# Revit family: Haworth_JiveTable_PebbleSymmetricalLegs
name_source: partatom
category: Furniture Systems
revit_build: Autodesk Revit 2018 (Build: 20170223_1515(x64)
units: mm (PartAtom-declared; Revit-internal decimal feet)

## family parameters
Always vertical = Yes
Cut with Voids When Loaded = No
OmniClass Number = 23.40.70.14.64.21
OmniClass Title = Systems Furniture
Part Type = Normal
Room Calculation Point = No
Round Connector Dimension = Use Diameter
Shared = No
Work Plane-Based = No

## types (19) — shared parameters
Assembly Code = E2020200
Custom Size = No
Manufacturer = Haworth, Inc.
Max. Height = 29"
Min. Height = 16"
Model = Hawoth Jive
Revision Number = 0
Size = Verify Final Dim. w/ Haworth
Standard Depths = 24, 30, 36, 42, 48, 54, 60 in.
Standard Height = 16, 20, 29 in.
Standard Widths = 24, 30, 36, 42, 48, 54, 60 in.
Table Thickness = 1 3/16"
URL = http://www.haworth.com
URL - Product = http://www.haworth.com
Warranty = http://haworth.com

## per-type parameters (varying)
- 24d 24w 16h - Post Extruded Base - With Glides: 24in x 24in=Yes; 30in x 30in=No; 36in x 36in=No; 42in x 42in=No; 48in x 48in=No; 54in x 54in=No; 60in x 60in=No; Actual Depth=24"; Actual Height=16"; Actual Width=24"; Casters=No; Controls Post Extruded 42d 42w Only=No; Controls Post Round 42d 42w Only=Yes; Depth=24"; Description=Haworth Jive Table Pebble Symmetrical Legs - 24d 24w 16h - Post Extruded Base - With Glides; Glides=Yes; Height=16"; Leg Distance x=5 215/256"; Leg Distance y=5 215/256"; Leg Height=14 13/16"; Post Extruded 42d 42w=No; Post Extruded Leg=Yes; Post Extruded Leg Table Types=Yes; Post Round 42d 42w=No; Post Round Leg=No; Post Round Leg Table Types=No; Width=24"
- 30d 30w 16h - Post Extruded Base - With Glides: 24in x 24in=No; 30in x 30in=Yes; 36in x 36in=No; 42in x 42in=No; 48in x 48in=No; 54in x 54in=No; 60in x 60in=No; Actual Depth=30"; Actual Height=16"; Actual Width=30"; Casters=No; Controls Post Extruded 42d 42w Only=No; Controls Post Round 42d 42w Only=Yes; Depth=30"; Description=Haworth Jive Table Pebble Symmetrical Legs - 30d 30w 16h - Post Extruded Base - With Glides; Glides=Yes; Height=16"; Leg Distance x=5 215/256"; Leg Distance y=5 215/256"; Leg Height=14 13/16"; Post Extruded 42d 42w=No; Post Extruded Leg=Yes; Post Extruded Leg Table Types=Yes; Post Round 42d 42w=No; Post Round Leg=No; Post Round Leg Table Types=No; Width=30"
- 36d 36w 16h - Post Extruded Base - With Glides: 24in x 24in=No; 30in x 30in=No; 36in x 36in=Yes; 42in x 42in=No; 48in x 48in=No; 54in x 54in=No; 60in x 60in=No; Actual Depth=36"; Actual Height=16"; Actual Width=36"; Casters=No; Controls Post Extruded 42d 42w Only=No; Controls Post Round 42d 42w Only=Yes; Depth=36"; Description=Haworth Jive Table Pebble Symmetrical Legs - 36d 36w 16h - Post Extruded Base - With Glides; Glides=Yes; Height=16"; Leg Distance x=12 215/256"; Leg Distance y=7 215/256"; Leg Height=14 13/16"; Post Extruded 42d 42w=No; Post Extruded Leg=Yes; Post Extruded Leg Table Types=Yes; Post Round 42d 42w=No; Post Round Leg=No; Post Round Leg Table Types=No; Width=36"
- 48d 48w 16h - Post Extruded Base - With Glides: 24in x 24in=No; 30in x 30in=No; 36in x 36in=No; 42in x 42in=No; 48in x 48in=Yes; 54in x 54in=No; 60in x 60in=No; Actual Depth=48"; Actual Height=16"; Actual Width=48"; Casters=No; Controls Post Extruded 42d 42w Only=No; Controls Post Round 42d 42w Only=Yes; Depth=48"; Description=Haworth Jive Table Pebble Symmetrical Legs - 48d 48w 16h - Post Extruded Base - With Glides; Glides=Yes; Height=16"; Leg Distance x=15 51/256"; Leg Distance y=15 51/256"; Leg Height=14 13/16"; Post Extruded 42d 42w=No; Post Extruded Leg=Yes; Post Extruded Leg Table Types=Yes; Post Round 42d 42w=No; Post Round Leg=No; Post Round Leg Table Types=No; Width=48"
- 24d 24w 20h - Post Extruded Base - With Glides: 24in x 24in=Yes; 30in x 30in=No; 36in x 36in=No; 42in x 42in=No; 48in x 48in=No; 54in x 54in=No; 60in x 60in=No; Actual Depth=24"; Actual Height=20"; Actual Width=24"; Casters=No; Controls Post Extruded 42d 42w Only=No; Controls Post Round 42d 42w Only=Yes; Depth=24"; Description=Haworth Jive Table Pebble Symmetrical Legs - 24d 24w 20h - Post Extruded Base - With Glides; Glides=Yes; Height=20"; Leg Distance x=5 215/256"; Leg Distance y=5 215/256"; Leg Height=18 13/16"; Post Extruded 42d 42w=No; Post Extruded Leg=Yes; Post Extruded Leg Table Types=Yes; Post Round 42d 42w=No; Post Round Leg=No; Post Round Leg Table Types=No; Width=24"
- 30d 30w 20h - Post Extruded Base - With Glides: 24in x 24in=No; 30in x 30in=Yes; 36in x 36in=No; 42in x 42in=No; 48in x 48in=No; 54in x 54in=No; 60in x 60in=No; Actual Depth=30"; Actual Height=20"; Actual Width=30"; Casters=No; Controls Post Extruded 42d 42w Only=No; Controls Post Round 42d 42w Only=Yes; Depth=30"; Description=Haworth Jive Table Pebble Symmetrical Legs - 30d 30w 20h - Post Extruded Base - With Glides; Glides=Yes; Height=20"; Leg Distance x=5 215/256"; Leg Distance y=5 215/256"; Leg Height=18 13/16"; Post Extruded 42d 42w=No; Post Extruded Leg=Yes; Post Extruded Leg Table Types=Yes; Post Round 42d 42w=No; Post Round Leg=No; Post Round Leg Table Types=No; Width=30"
- 36d 36w 20h - Post Extruded Base - With Glides: 24in x 24in=No; 30in x 30in=No; 36in x 36in=Yes; 42in x 42in=No; 48in x 48in=No; 54in x 54in=No; 60in x 60in=No; Actual Depth=36"; Actual Height=20"; Actual Width=36"; Casters=No; Controls Post Extruded 42d 42w Only=No; Controls Post Round 42d 42w Only=Yes; Depth=36"; Description=Haworth Jive Table Pebble Symmetrical Legs - 36d 36w 20h - Post Extruded Base - With Glides; Glides=Yes; Height=20"; Leg Distance x=12 215/256"; Leg Distance y=7 215/256"; Leg Height=18 13/16"; Post Extruded 42d 42w=No; Post Extruded Leg=Yes; Post Extruded Leg Table Types=Yes; Post Round 42d 42w=No; Post Round Leg=No; Post Round Leg Table Types=No; Width=36"
- 48d 48w 20h - Post Extruded Base - With Glides: 24in x 24in=No; 30in x 30in=No; 36in x 36in=No; 42in x 42in=No; 48in x 48in=Yes; 54in x 54in=No; 60in x 60in=No; Actual Depth=48"; Actual Height=20"; Actual Width=48"; Casters=No; Controls Post Extruded 42d 42w Only=No; Controls Post Round 42d 42w Only=Yes; Depth=48"; Description=Haworth Jive Table Pebble Symmetrical Legs - 48d 48w 20h - Post Extruded Base - With Glides; Glides=Yes; Height=20"; Leg Distance x=15 51/256"; Leg Distance y=15 51/256"; Leg Height=18 13/16"; Post Extruded 42d 42w=No; Post Extruded Leg=Yes; Post Extruded Leg Table Types=Yes; Post Round 42d 42w=No; Post Round Leg=No; Post Round Leg Table Types=No; Width=48"
- 42d 42w 29h - Post Extruded Base - With Casters: 24in x 24in=No; 30in x 30in=No; 36in x 36in=No; 42in x 42in=Yes; 48in x 48in=No; 54in x 54in=No; 60in x 60in=No; Actual Depth=42"; Actual Height=29"; Actual Width=42"; Casters=Yes; Controls Post Extruded 42d 42w Only=Yes; Controls Post Round 42d 42w Only=No; Depth=42"; Description=Haworth Jive Table Pebble Symmetrical Legs - 42d 42w 29h - Post Extruded Base - With Casters; Glides=No; Height=29"; Leg Distance x=12 215/256"; Leg Distance y=12 215/256"; Leg Height=27 13/16"; Post Extruded 42d 42w=Yes; Post Extruded Leg=Yes; Post Extruded Leg Table Types=Yes; Post Round 42d 42w=No; Post Round Leg=No; Post Round Leg Table Types=No; Width=42"
- 48d 48w 29h - Post Extruded Base - With Casters: 24in x 24in=No; 30in x 30in=No; 36in x 36in=No; 42in x 42in=No; 48in x 48in=Yes; 54in x 54in=No; 60in x 60in=No; Actual Depth=48"; Actual Height=29"; Actual Width=48"; Casters=Yes; Controls Post Extruded 42d 42w Only=No; Controls Post Round 42d 42w Only=Yes; Depth=48"; Description=Haworth Jive Table Pebble Symmetrical Legs - 48d 48w 29h - Post Extruded Base - With Casters; Glides=No; Height=29"; Leg Distance x=15 51/256"; Leg Distance y=15 51/256"; Leg Height=27 13/16"; Post Extruded 42d 42w=No; Post Extruded Leg=Yes; Post Extruded Leg Table Types=Yes; Post Round 42d 42w=No; Post Round Leg=No; Post Round Leg Table Types=No; Width=48"
- 54d 54w 29h - Post Extruded Base - With Casters: 24in x 24in=No; 30in x 30in=No; 36in x 36in=No; 42in x 42in=No; 48in x 48in=No; 54in x 54in=Yes; 60in x 60in=No; Actual Depth=54"; Actual Height=29"; Actual Width=54"; Casters=Yes; Controls Post Extruded 42d 42w Only=No; Controls Post Round 42d 42w Only=Yes; Depth=54"; Description=Haworth Jive Table Pebble Symmetrical Legs - 54d 54w 29h - Post Extruded Base - With Casters; Glides=No; Height=29"; Leg Distance x=17 123/256"; Leg Distance y=17 123/256"; Leg Height=27 13/16"; Post Extruded 42d 42w=No; Post Extruded Leg=Yes; Post Extruded Leg Table Types=Yes; Post Round 42d 42w=No; Post Round Leg=No; Post Round Leg Table Types=No; Width=54"
- 42d 42w 29h - Post Extruded Base - With Glides: 24in x 24in=No; 30in x 30in=No; 36in x 36in=No; 42in x 42in=Yes; 48in x 48in=No; 54in x 54in=No; 60in x 60in=No; Actual Depth=42"; Actual Height=29"; Actual Width=42"; Casters=No; Controls Post Extruded 42d 42w Only=Yes; Controls Post Round 42d 42w Only=No; Depth=42"; Description=Haworth Jive Table Pebble Symmetrical Legs - 42d 42w 29h - Post Extruded Base - With Glides; Glides=Yes; Height=29"; Leg Distance x=12 215/256"; Leg Distance y=12 215/256"; Leg Height=27 13/16"; Post Extruded 42d 42w=Yes; Post Extruded Leg=Yes; Post Extruded Leg Table Types=Yes; Post Round 42d 42w=No; Post Round Leg=No; Post Round Leg Table Types=No; Width=42"
- 48d 48w 29h - Post Extruded Base - With Glides: 24in x 24in=No; 30in x 30in=No; 36in x 36in=No; 42in x 42in=No; 48in x 48in=Yes; 54in x 54in=No; 60in x 60in=No; Actual Depth=48"; Actual Height=29"; Actual Width=48"; Casters=No; Controls Post Extruded 42d 42w Only=No; Controls Post Round 42d 42w Only=Yes; Depth=48"; Description=Haworth Jive Table Pebble Symmetrical Legs - 48d 48w 29h - Post Extruded Base - With Glides; Glides=Yes; Height=29"; Leg Distance x=15 51/256"; Leg Distance y=15 51/256"; Leg Height=27 13/16"; Post Extruded 42d 42w=No; Post Extruded Leg=Yes; Post Extruded Leg Table Types=Yes; Post Round 42d 42w=No; Post Round Leg=No; Post Round Leg Table Types=No; Width=48"
- 54d 54w 29h - Post Extruded Base - With Glides: 24in x 24in=No; 30in x 30in=No; 36in x 36in=No; 42in x 42in=No; 48in x 48in=No; 54in x 54in=Yes; 60in x 60in=No; Actual Depth=54"; Actual Height=29"; Actual Width=54"; Casters=No; Controls Post Extruded 42d 42w Only=No; Controls Post Round 42d 42w Only=Yes; Depth=54"; Description=Haworth Jive Table Pebble Symmetrical Legs - 54d 54w 29h - Post Extruded Base - With Glides; Glides=Yes; Height=29"; Leg Distance x=17 123/256"; Leg Distance y=17 123/256"; Leg Height=27 13/16"; Post Extruded 42d 42w=No; Post Extruded Leg=Yes; Post Extruded Leg Table Types=Yes; Post Round 42d 42w=No; Post Round Leg=No; Post Round Leg Table Types=No; Width=54"
- 60d 60w 29h - Post Extruded Base - With Glides: 24in x 24in=No; 30in x 30in=No; 36in x 36in=No; 42in x 42in=No; 48in x 48in=No; 54in x 54in=No; 60in x 60in=Yes; Actual Depth=60"; Actual Height=29"; Actual Width=60"; Casters=No; Controls Post Extruded 42d 42w Only=No; Controls Post Round 42d 42w Only=Yes; Depth=60"; Description=Haworth Jive Table Pebble Symmetrical Legs - 60d 60w 29h - Post Extruded Base - With Glides; Glides=Yes; Height=29"; Leg Distance x=19 83/128"; Leg Distance y=19 83/128"; Leg Height=27 13/16"; Post Extruded 42d 42w=No; Post Extruded Leg=Yes; Post Extruded Leg Table Types=Yes; Post Round 42d 42w=No; Post Round Leg=No; Post Round Leg Table Types=No; Width=60"
- 42d 42w 29h - Post Round Base - With Casters: 24in x 24in=No; 30in x 30in=No; 36in x 36in=No; 42in x 42in=Yes; 48in x 48in=No; 54in x 54in=No; 60in x 60in=No; Actual Depth=42"; Actual Height=29"; Actual Width=42"; Casters=Yes; Controls Post Extruded 42d 42w Only=No; Controls Post Round 42d 42w Only=Yes; Depth=42"; Description=Haworth Jive Table Pebble Symmetrical Legs - 42d 42w 29h - Post Round Base - With Casters; Glides=No; Height=29"; Leg Distance x=12 215/256"; Leg Distance y=12 215/256"; Leg Height=27 13/16"; Post Extruded 42d 42w=No; Post Extruded Leg=No; Post Extruded Leg Table Types=No; Post Round 42d 42w=Yes; Post Round Leg=Yes; Post Round Leg Table Types=Yes; Width=42"
- 42d 42w 29h - Post Round Base - With Glides: 24in x 24in=No; 30in x 30in=No; 36in x 36in=No; 42in x 42in=Yes; 48in x 48in=No; 54in x 54in=No; 60in x 60in=No; Actual Depth=42"; Actual Height=29"; Actual Width=42"; Casters=No; Controls Post Extruded 42d 42w Only=No; Controls Post Round 42d 42w Only=Yes; Depth=42"; Description=Haworth Jive Table Pebble Symmetrical Legs - 42d 42w 29h - Post Round Base - With Glides; Glides=Yes; Height=29"; Leg Distance x=12 215/256"; Leg Distance y=12 215/256"; Leg Height=27 13/16"; Post Extruded 42d 42w=No; Post Extruded Leg=No; Post Extruded Leg Table Types=No; Post Round 42d 42w=Yes; Post Round Leg=Yes; Post Round Leg Table Types=Yes; Width=42"
- 48d 48w 29h - Post Round Base - With Casters: 24in x 24in=No; 30in x 30in=No; 36in x 36in=No; 42in x 42in=No; 48in x 48in=Yes; 54in x 54in=No; 60in x 60in=No; Actual Depth=48"; Actual Height=29"; Actual Width=48"; Casters=Yes; Controls Post Extruded 42d 42w Only=No; Controls Post Round 42d 42w Only=Yes; Depth=48"; Description=Haworth Jive Table Pebble Symmetrical Legs - 48d 48w 29h - Post Round Base - With Casters; Glides=No; Height=29"; Leg Distance x=15 51/256"; Leg Distance y=15 51/256"; Leg Height=27 13/16"; Post Extruded 42d 42w=No; Post Extruded Leg=Yes; Post Extruded Leg Table Types=Yes; Post Round 42d 42w=No; Post Round Leg=No; Post Round Leg Table Types=No; Width=48"
- 48d 48w 29h - Post Round Base - With Glides: 24in x 24in=No; 30in x 30in=No; 36in x 36in=No; 42in x 42in=No; 48in x 48in=Yes; 54in x 54in=No; 60in x 60in=No; Actual Depth=48"; Actual Height=29"; Actual Width=48"; Casters=No; Controls Post Extruded 42d 42w Only=No; Controls Post Round 42d 42w Only=Yes; Depth=48"; Description=Haworth Jive Table Pebble Symmetrical Legs - 48d 48w 29h - Post Round Base - With Glides; Glides=Yes; Height=29"; Leg Distance x=15 51/256"; Leg Distance y=15 51/256"; Leg Height=27 13/16"; Post Extruded 42d 42w=No; Post Extruded Leg=Yes; Post Extruded Leg Table Types=Yes; Post Round 42d 42w=No; Post Round Leg=No; Post Round Leg Table Types=No; Width=48"

## geometry (parser evidence)
native form markers: Sweep x27
no freeform markers — native parametric forms only
